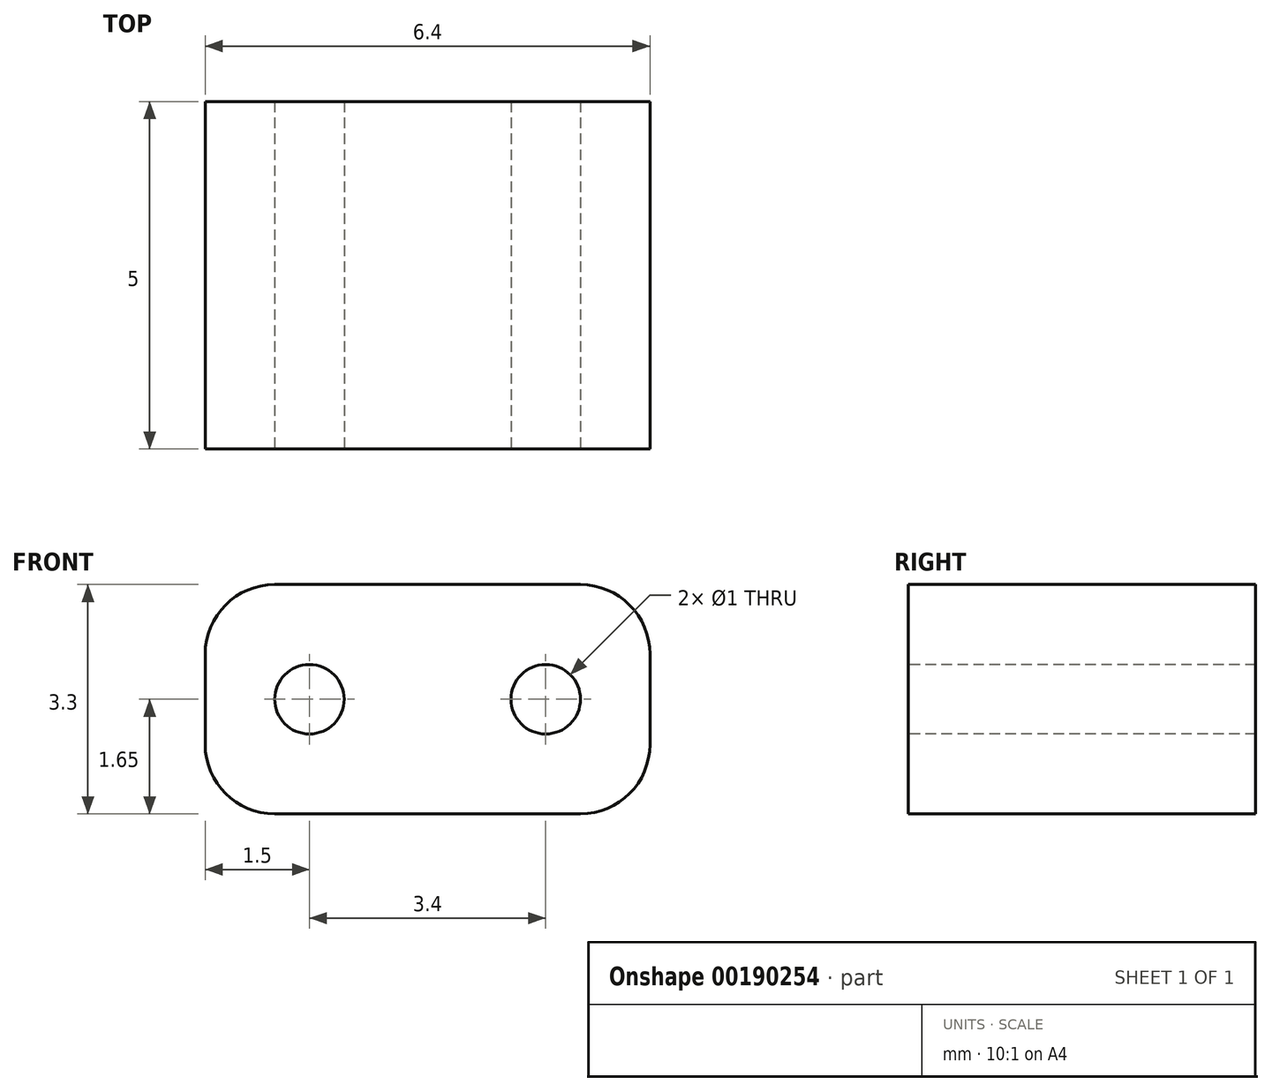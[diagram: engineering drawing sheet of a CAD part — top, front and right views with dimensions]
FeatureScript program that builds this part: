
annotation { "Feature Type Name" : "Feature", "Feature Type Description" : "" }
export const myFeature = defineFeature(function(context is Context, id is Id, definition is map)
    precondition{}
    {
        {
            var Q0;
            Q0=qCreatedBy(makeId("Top.planeOp"),FACE);
            var sketch = newSketch(context, id + "F0", { "sketchPlane" : qUnion([Q0])});
            skLineSegment(sketch, "E0.bottom", {"start": v(0, 0) * mm, "end": v(6.4, 0) * mm});
            skLineSegment(sketch, "E0.top", {"start": v(0, 5) * mm, "end": v(6.4, 5) * mm});
            skLineSegment(sketch, "E0.left", {"start": v(0, 0) * mm, "end": v(0, 5) * mm});
            skLineSegment(sketch, "E0.right", {"start": v(6.4, 0) * mm, "end": v(6.4, 5) * mm});
            skSolve(sketch);
        }
        {
            var Q0;
            Q0=makeQuery(id+"F0.imprint","IMPRINT",FACE,{"disambiguationData":[TD([[makeQuery(id+"F0.imprint","IMPRINT",EDGE,{"derivedFrom":sQuery(id+"F0.wireOp",EDGE,"E0.bottom")}),1.0]])]});
            extrude(context, id + "F1", {"entities" : qUnion([Q0]), "depth" : 3.3 * mm});
        }
        {
            var Q0;
            Q0=makeQuery(id+"F1.opExtrude","CAP_EDGE",EDGE,{"disambiguationData":[OSD([sQuery(id+"F0.wireOp",EDGE,"E0.left")])],"isStart":false});
            var Q1;
            Q1=makeQuery(id+"F1.opExtrude","CAP_EDGE",EDGE,{"disambiguationData":[OSD([sQuery(id+"F0.wireOp",EDGE,"E0.right")])],"isStart":false});
            var Q2;
            Q2=makeQuery(id+"F1.opExtrude","CAP_EDGE",EDGE,{"disambiguationData":[OSD([sQuery(id+"F0.wireOp",EDGE,"E0.right")])],"isStart":true});
            var Q3;
            Q3=makeQuery(id+"F1.opExtrude","CAP_EDGE",EDGE,{"disambiguationData":[OSD([sQuery(id+"F0.wireOp",EDGE,"E0.left")])],"isStart":true});
            fillet(context, id + "F2", {"entities" : qUnion([Q0, Q1, Q2, Q3]), "radius" : 1 * mm, "tangentPropagation" : true, "allowEdgeOverflow" : false});
        }
        {
            var Q0;
            Q0=makeQuery(id+"F1.opExtrude","SWEPT_FACE",FACE,{"disambiguationData":[OSD([sQuery(id+"F0.wireOp",EDGE,"E0.bottom")])]});
            var sketch = newSketch(context, id + "F3", { "sketchPlane" : qUnion([Q0])});
            skCircle(sketch, "E1", {"center": v(1.5, 1.65) * mm, "radius": 0.5 * mm});
            skLineSegment(sketch, "E2", {"start": v(1.5, 1.65) * mm, "end": v(0, 1.65) * mm, "construction": true});
            skLineSegment(sketch, "E3", {"start": v(3.2, 3.3) * mm, "end": v(3.2, 0) * mm, "construction": true});
            skCircle(sketch, "E4.MirrorC", {"center": v(4.9, 1.65) * mm, "radius": 0.5 * mm});
            skSolve(sketch);
        }
        {
            var Q0;
            Q0 = qSketchRegion(id + "F3", true);
            extrude(context, id + "F4", {"entities" : qUnion([Q0]), "operationType" : NewBodyOperationType.REMOVE, "endBound" : BoundingType.THROUGH_ALL, "oppositeDirection" : true, "depth" : 25 * mm});
        }
    });
